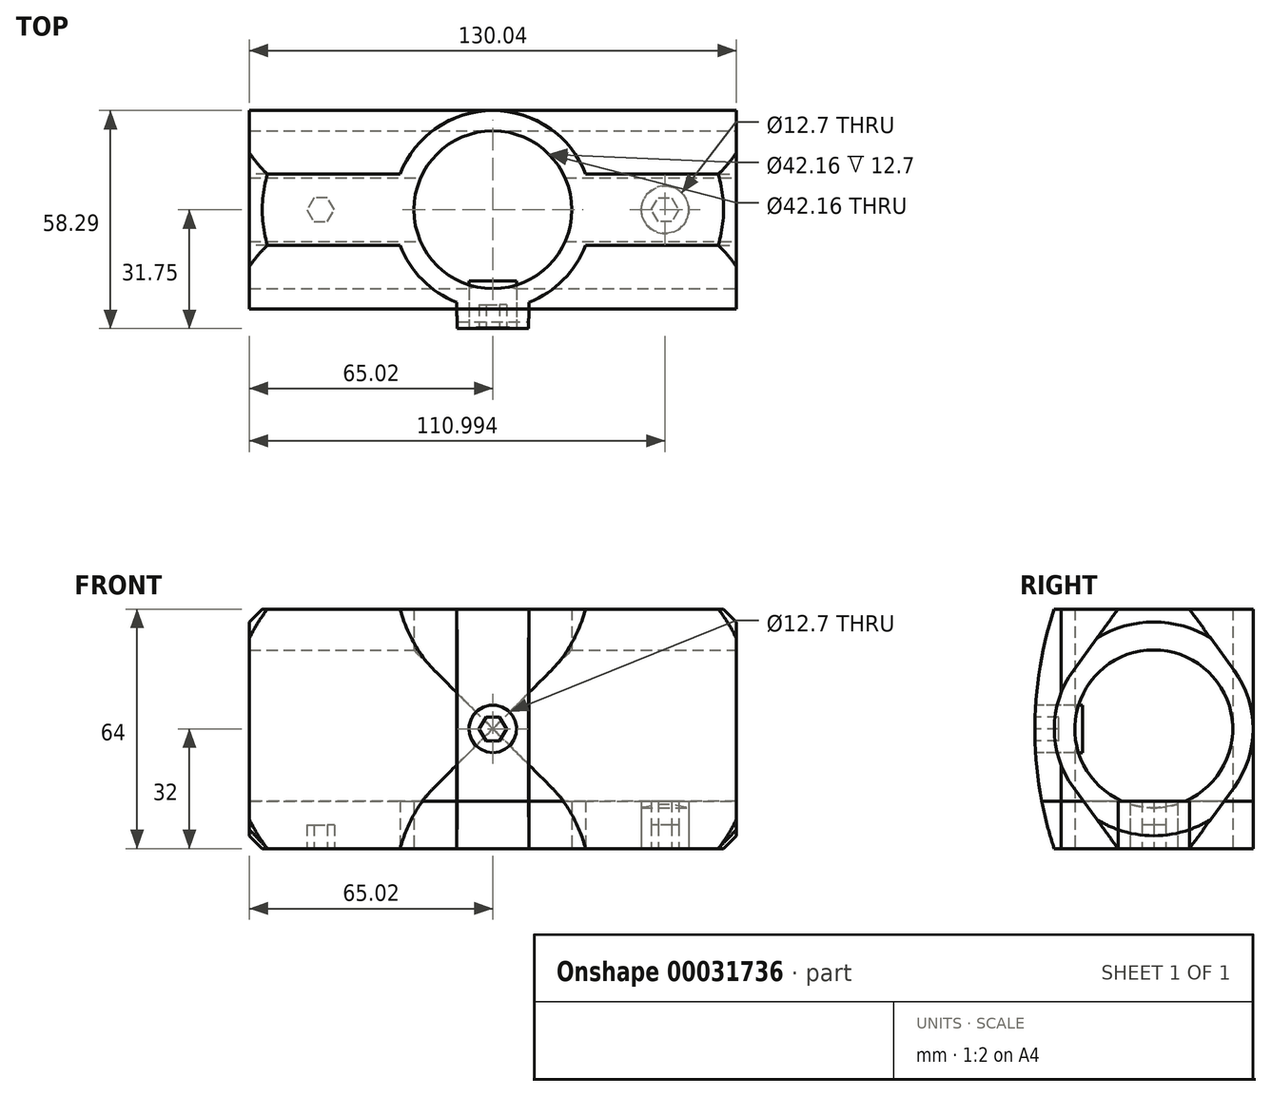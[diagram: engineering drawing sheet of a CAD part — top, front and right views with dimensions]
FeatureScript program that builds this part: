
annotation { "Feature Type Name" : "Feature", "Feature Type Description" : "" }
export const myFeature = defineFeature(function(context is Context, id is Id, definition is map)
    precondition{}
    {
        {
            var Q0;
            Q0=qCreatedBy(makeId("Right.planeOp"),FACE);
            var sketch = newSketch(context, id + "F0", { "sketchPlane" : qUnion([Q0])});
            skCircle(sketch, "E0", {"center": v(0, 0) * mm, "radius": 21.08 * mm});
            skCircle(sketch, "E1", {"center": v(0, 0) * mm, "radius": 26.54 * mm});
            skLineSegment(sketch, "E2.rect.bottom", {"start": v(9.53, 32) * mm, "end": v(-9.53, 32) * mm});
            skLineSegment(sketch, "E2.rect.top", {"start": v(9.53, -32) * mm, "end": v(-9.53, -32) * mm});
            skLineSegment(sketch, "E2.rect.left", {"start": v(9.53, 32) * mm, "end": v(9.53, -32) * mm});
            skLineSegment(sketch, "E2.rect.right", {"start": v(-9.53, 32) * mm, "end": v(-9.53, -32) * mm});
            skLineSegment(sketch, "E3", {"start": v(-9.53, 32) * mm, "end": v(-21.45, 15.63) * mm});
            skLineSegment(sketch, "E4", {"start": v(9.52, 32) * mm, "end": v(21.45, 15.63) * mm});
            skLineSegment(sketch, "E5", {"start": v(-9.52, -32) * mm, "end": v(-21.45, -15.63) * mm});
            skLineSegment(sketch, "E6", {"start": v(9.52, -32) * mm, "end": v(21.45, -15.63) * mm});
            skSolve(sketch);
        }
        {
            var Q0;
            {var subQ0=sQuery(id+"F0.wireOp",EDGE,"E2.rect.right");var subQ1=sQuery(id+"F0.wireOp",EDGE,"E0");var subQ3=makeQuery(id+"F0.imprint","INTERSECT",VERTEX,{"disambiguationData":[OD(0.0)],"derivedFrom":[subQ1,subQ0]});Q0=makeQuery(id+"F0.imprint","IMPRINT",FACE,{"disambiguationData":[TD([[makeQuery(id+"F0.imprint","IMPRINT",EDGE,{"disambiguationData":[TD([[subQ3,1.0]])],"derivedFrom":subQ1}),1.0]])]});}
            var Q1;
            {var subQ0=sQuery(id+"F0.wireOp",EDGE,"E2.rect.right");var subQ1=sQuery(id+"F0.wireOp",EDGE,"E0");var subQ3=makeQuery(id+"F0.imprint","INTERSECT",VERTEX,{"disambiguationData":[OD(0.0)],"derivedFrom":[subQ1,subQ0]});Q1=makeQuery(id+"F0.imprint","IMPRINT",FACE,{"disambiguationData":[TD([[makeQuery(id+"F0.imprint","IMPRINT",EDGE,{"disambiguationData":[TD([[subQ3,-1.0]])],"derivedFrom":subQ1}),1.0]])]});}
            var Q2;
            {var subQ0=sQuery(id+"F0.wireOp",EDGE,"E2.rect.right");var subQ3=sQuery(id+"F0.wireOp",EDGE,"E0");var subQ4=makeQuery(id+"F0.imprint","INTERSECT",VERTEX,{"disambiguationData":[OD(0.0)],"derivedFrom":[subQ3,subQ0]});Q2=makeQuery(id+"F0.imprint","IMPRINT",FACE,{"disambiguationData":[TD([[makeQuery(id+"F0.imprint","IMPRINT",EDGE,{"disambiguationData":[TD([[subQ4,-1.0]])],"derivedFrom":subQ3}),-1.0]])]});}
            var Q3;
            {var subQ0=sQuery(id+"F0.wireOp",EDGE,"E5");Q3=makeQuery(id+"F0.imprint","IMPRINT",FACE,{"disambiguationData":[TD([[makeQuery(id+"F0.imprint","IMPRINT",EDGE,{"derivedFrom":subQ0}),-1.0]])]});}
            var Q4;
            {var subQ3=sQuery(id+"F0.wireOp",EDGE,"E2.rect.top");Q4=makeQuery(id+"F0.imprint","IMPRINT",FACE,{"disambiguationData":[TD([[makeQuery(id+"F0.imprint","IMPRINT",EDGE,{"derivedFrom":subQ3}),-1.0]])]});}
            var Q5;
            {var subQ0=sQuery(id+"F0.wireOp",EDGE,"E2.rect.right");var subQ3=sQuery(id+"F0.wireOp",EDGE,"E0");var subQ4=makeQuery(id+"F0.imprint","INTERSECT",VERTEX,{"disambiguationData":[OD(1.0)],"derivedFrom":[subQ3,subQ0]});Q5=makeQuery(id+"F0.imprint","IMPRINT",FACE,{"disambiguationData":[TD([[makeQuery(id+"F0.imprint","IMPRINT",EDGE,{"disambiguationData":[TD([[subQ4,-1.0]])],"derivedFrom":subQ3}),-1.0]])]});}
            var Q6;
            {var subQ0=sQuery(id+"F0.wireOp",EDGE,"E6");Q6=makeQuery(id+"F0.imprint","IMPRINT",FACE,{"disambiguationData":[TD([[makeQuery(id+"F0.imprint","IMPRINT",EDGE,{"derivedFrom":subQ0}),1.0]])]});}
            var Q7;
            {var subQ0=sQuery(id+"F0.wireOp",EDGE,"E2.rect.left");var subQ3=sQuery(id+"F0.wireOp",EDGE,"E0");var subQ4=makeQuery(id+"F0.imprint","INTERSECT",VERTEX,{"disambiguationData":[OD(0.0)],"derivedFrom":[subQ3,subQ0]});Q7=makeQuery(id+"F0.imprint","IMPRINT",FACE,{"disambiguationData":[TD([[makeQuery(id+"F0.imprint","IMPRINT",EDGE,{"disambiguationData":[TD([[subQ4,1.0]])],"derivedFrom":subQ3}),-1.0]])]});}
            var Q8;
            {var subQ0=sQuery(id+"F0.wireOp",EDGE,"E2.rect.left");var subQ1=sQuery(id+"F0.wireOp",EDGE,"E0");var subQ3=makeQuery(id+"F0.imprint","INTERSECT",VERTEX,{"disambiguationData":[OD(0.0)],"derivedFrom":[subQ1,subQ0]});Q8=makeQuery(id+"F0.imprint","IMPRINT",FACE,{"disambiguationData":[TD([[makeQuery(id+"F0.imprint","IMPRINT",EDGE,{"disambiguationData":[TD([[subQ3,1.0]])],"derivedFrom":subQ1}),1.0]])]});}
            var Q9;
            {var subQ0=sQuery(id+"F0.wireOp",EDGE,"E2.rect.right");var subQ3=sQuery(id+"F0.wireOp",EDGE,"E0");var subQ4=makeQuery(id+"F0.imprint","INTERSECT",VERTEX,{"disambiguationData":[OD(0.0)],"derivedFrom":[subQ3,subQ0]});Q9=makeQuery(id+"F0.imprint","IMPRINT",FACE,{"disambiguationData":[TD([[makeQuery(id+"F0.imprint","IMPRINT",EDGE,{"disambiguationData":[TD([[subQ4,1.0]])],"derivedFrom":subQ3}),-1.0]])]});}
            var Q10;
            {var subQ0=sQuery(id+"F0.wireOp",EDGE,"E4");Q10=makeQuery(id+"F0.imprint","IMPRINT",FACE,{"disambiguationData":[TD([[makeQuery(id+"F0.imprint","IMPRINT",EDGE,{"derivedFrom":subQ0}),-1.0]])]});}
            var Q11;
            {var subQ3=sQuery(id+"F0.wireOp",EDGE,"E2.rect.bottom");Q11=makeQuery(id+"F0.imprint","IMPRINT",FACE,{"disambiguationData":[TD([[makeQuery(id+"F0.imprint","IMPRINT",EDGE,{"derivedFrom":subQ3}),1.0]])]});}
            var Q12;
            {var subQ0=sQuery(id+"F0.wireOp",EDGE,"E3");Q12=makeQuery(id+"F0.imprint","IMPRINT",FACE,{"disambiguationData":[TD([[makeQuery(id+"F0.imprint","IMPRINT",EDGE,{"derivedFrom":subQ0}),1.0]])]});}
            extrude(context, id + "F1", {"entities" : qUnion([Q0, Q1, Q2, Q3, Q4, Q5, Q6, Q7, Q8, Q9, Q10, Q11, Q12]), "endBound" : BoundingType.SYMMETRIC, "depth" : 130.05 * mm});
        }
        {
            var Q0;
            Q0=qCreatedBy(makeId("Top.planeOp"),FACE);
            var sketch = newSketch(context, id + "F2", { "sketchPlane" : qUnion([Q0])});
            skCircle(sketch, "E7", {"center": v(0, 0) * mm, "radius": 26.54 * mm});
            skCircle(sketch, "E8", {"center": v(0, 0) * mm, "radius": 21.08 * mm});
            skLineSegment(sketch, "E9", {"start": v(0, -31.75) * mm, "end": v(-9.53, -31.75) * mm});
            skLineSegment(sketch, "E10", {"start": v(-9.53, -31.75) * mm, "end": v(-9.67, -24.72) * mm});
            skLineSegment(sketch, "E11", {"start": v(-9.67, -24.72) * mm, "end": v(0, -24.72) * mm});
            skLineSegment(sketch, "E12.MirrorCS", {"start": v(0, -31.75) * mm, "end": v(9.53, -31.75) * mm});
            skLineSegment(sketch, "E13.MirrorCS", {"start": v(9.52, -31.75) * mm, "end": v(9.67, -24.72) * mm});
            skLineSegment(sketch, "E14.MirrorCS", {"start": v(9.67, -24.72) * mm, "end": v(0, -24.72) * mm});
            skSolve(sketch);
        }
        {
            var Q0;
            Q0=makeQuery(id+"F2.imprint","IMPRINT",FACE,{"disambiguationData":[TD([[makeQuery(id+"F2.imprint","IMPRINT",EDGE,{"derivedFrom":sQuery(id+"F2.wireOp",EDGE,"E9")}),-1.0]])]});
            var Q1;
            {var subQ1=sQuery(id+"F2.wireOp",EDGE,"E11");Q1=makeQuery(id+"F2.imprint","IMPRINT",FACE,{"disambiguationData":[TD([[makeQuery(id+"F2.imprint","IMPRINT",EDGE,{"derivedFrom":subQ1}),-1.0]])]});}
            var Q2;
            Q2=makeQuery(id+"F2.imprint","IMPRINT",FACE,{"disambiguationData":[TD([[makeQuery(id+"F2.imprint","IMPRINT",EDGE,{"derivedFrom":sQuery(id+"F2.wireOp",EDGE,"E8")}),-1.0]])]});
            var Q3;
            Q3=makeQuery(id+"F2.imprint","IMPRINT",FACE,{"disambiguationData":[TD([[makeQuery(id+"F2.imprint","IMPRINT",EDGE,{"derivedFrom":sQuery(id+"F2.wireOp",EDGE,"E8")}),1.0]])]});
            var Q4;
            Q4=makeQuery(id+"F1.opExtrude","SWEPT_FACE",FACE,{"disambiguationData":[OSD([sQuery(id+"F0.wireOp",EDGE,"E2.rect.bottom")])]});
            var Q5;
            Q5=makeQuery(id+"F1.opExtrude","SWEPT_FACE",FACE,{"disambiguationData":[OSD([sQuery(id+"F0.wireOp",EDGE,"E2.rect.top")])]});
            extrude(context, id + "F3", {"entities" : qUnion([Q0, Q1, Q2, Q3]), "operationType" : NewBodyOperationType.ADD, "endBound" : BoundingType.UP_TO_SURFACE, "endBoundEntityFace" : qUnion([Q4]), "depth" : 25.4 * mm, "hasSecondDirection" : true, "secondDirectionBound" : SecondDirectionBoundingType.UP_TO_SURFACE, "secondDirectionOppositeDirection" : true, "secondDirectionBoundEntityFace" : qUnion([Q5]), "secondDirectionDepth" : 25.4 * mm});
        }
        {
            var Q0;
            {var subQ0=sQuery(id+"F0.wireOp",EDGE,"E2.rect.left");var subQ1=sQuery(id+"F0.wireOp",EDGE,"E0");var subQ3=makeQuery(id+"F0.imprint","INTERSECT",VERTEX,{"disambiguationData":[OD(0.0)],"derivedFrom":[subQ1,subQ0]});Q0=makeQuery(id+"F0.imprint","IMPRINT",FACE,{"disambiguationData":[TD([[makeQuery(id+"F0.imprint","IMPRINT",EDGE,{"disambiguationData":[TD([[subQ3,1.0]])],"derivedFrom":subQ1}),1.0]])]});}
            var Q1;
            {var subQ0=sQuery(id+"F0.wireOp",EDGE,"E2.rect.right");var subQ1=sQuery(id+"F0.wireOp",EDGE,"E0");var subQ3=makeQuery(id+"F0.imprint","INTERSECT",VERTEX,{"disambiguationData":[OD(0.0)],"derivedFrom":[subQ1,subQ0]});Q1=makeQuery(id+"F0.imprint","IMPRINT",FACE,{"disambiguationData":[TD([[makeQuery(id+"F0.imprint","IMPRINT",EDGE,{"disambiguationData":[TD([[subQ3,1.0]])],"derivedFrom":subQ1}),1.0]])]});}
            var Q2;
            {var subQ0=sQuery(id+"F0.wireOp",EDGE,"E2.rect.right");var subQ1=sQuery(id+"F0.wireOp",EDGE,"E0");var subQ3=makeQuery(id+"F0.imprint","INTERSECT",VERTEX,{"disambiguationData":[OD(0.0)],"derivedFrom":[subQ1,subQ0]});Q2=makeQuery(id+"F0.imprint","IMPRINT",FACE,{"disambiguationData":[TD([[makeQuery(id+"F0.imprint","IMPRINT",EDGE,{"disambiguationData":[TD([[subQ3,-1.0]])],"derivedFrom":subQ1}),1.0]])]});}
            extrude(context, id + "F4", {"entities" : qUnion([Q0, Q1, Q2]), "operationType" : NewBodyOperationType.REMOVE, "endBound" : BoundingType.THROUGH_ALL, "oppositeDirection" : true, "depth" : 25.4 * mm, "hasSecondDirection" : true, "secondDirectionBound" : SecondDirectionBoundingType.THROUGH_ALL, "secondDirectionOppositeDirection" : false, "secondDirectionDepth" : 25.4 * mm});
        }
        {
            var Q0;
            Q0=makeQuery(id+"F2.imprint","IMPRINT",FACE,{"disambiguationData":[TD([[makeQuery(id+"F2.imprint","IMPRINT",EDGE,{"derivedFrom":sQuery(id+"F2.wireOp",EDGE,"E8")}),1.0]])]});
            extrude(context, id + "F5", {"entities" : qUnion([Q0]), "operationType" : NewBodyOperationType.REMOVE, "endBound" : BoundingType.THROUGH_ALL, "depth" : 25.4 * mm, "hasSecondDirection" : true, "secondDirectionBound" : SecondDirectionBoundingType.THROUGH_ALL, "secondDirectionOppositeDirection" : true, "secondDirectionDepth" : 25.4 * mm});
        }
        {
            var Q0;
            Q0=makeQuery(id+"F3.opExtrude","SWEPT_FACE",FACE,{"disambiguationData":[OSD([sQuery(id+"F2.wireOp",EDGE,"E9"),sQuery(id+"F2.wireOp",EDGE,"E12.MirrorCS")])]});
            var sketch = newSketch(context, id + "F6", { "sketchPlane" : qUnion([Q0])});
            skCircle(sketch, "E15", {"center": v(0, 0) * mm, "radius": 6.35 * mm});
            skCircle(sketch, "E16.cCircle", {"center": v(0, 0) * mm, "radius": 3.18 * mm, "construction": true});
            skLineSegment(sketch, "E16.0", {"start": v(-1.83, 3.18) * mm, "end": v(1.83, 3.18) * mm});
            skLineSegment(sketch, "E16.1", {"start": v(1.83, 3.18) * mm, "end": v(3.67, 0) * mm});
            skLineSegment(sketch, "E16.2", {"start": v(3.67, 0) * mm, "end": v(1.83, -3.18) * mm});
            skLineSegment(sketch, "E16.3", {"start": v(1.83, -3.18) * mm, "end": v(-1.83, -3.18) * mm});
            skLineSegment(sketch, "E16.4", {"start": v(-1.83, -3.18) * mm, "end": v(-3.67, 0) * mm});
            skLineSegment(sketch, "E16.5", {"start": v(-3.67, 0) * mm, "end": v(-1.83, 3.18) * mm});
            skPoint(sketch, "E16.0.midPoint", {"position": v(0, 3.18) * mm});
            skSolve(sketch);
        }
        {
            var Q0;
            Q0=makeQuery(id+"F6.imprint","IMPRINT",FACE,{"disambiguationData":[TD([[makeQuery(id+"F6.imprint","IMPRINT",EDGE,{"derivedFrom":sQuery(id+"F6.wireOp",EDGE,"E16.0")}),-1.0]])]});
            var Q1;
            Q1=makeQuery(id+"F6.imprint","IMPRINT",FACE,{"disambiguationData":[TD([[makeQuery(id+"F6.imprint","IMPRINT",EDGE,{"derivedFrom":sQuery(id+"F6.wireOp",EDGE,"E15")}),1.0]])]});
            extrude(context, id + "F7", {"entities" : qUnion([Q0, Q1]), "oppositeDirection" : true, "depth" : 12.7 * mm});
        }
        {
            var Q0;
            Q0=makeQuery(id+"F3.boolean.opBoolean","MERGE",FACE,{"derivedFrom":[makeQuery(id+"F1.opExtrude","SWEPT_FACE",FACE,{"disambiguationData":[OSD([sQuery(id+"F0.wireOp",EDGE,"E2.rect.top")])]}),makeQuery(id+"F3.opExtrude","CAP_FACE",FACE,{"disambiguationData":[OSD([sQuery(id+"F2.wireOp",EDGE,"E7"),sQuery(id+"F2.wireOp",EDGE,"E9"),sQuery(id+"F2.wireOp",EDGE,"E10"),sQuery(id+"F2.wireOp",EDGE,"E12.MirrorCS"),sQuery(id+"F2.wireOp",EDGE,"E13.MirrorCS")])],"isStart":true})]});
            var sketch = newSketch(context, id + "F8", { "sketchPlane" : qUnion([Q0])});
            skCircle(sketch, "E17", {"center": v(-45.97, 0) * mm, "radius": 6.35 * mm});
            skCircle(sketch, "E18.cCircle", {"center": v(-45.97, 0) * mm, "radius": 3.18 * mm, "construction": true});
            skLineSegment(sketch, "E18.0", {"start": v(-47.8, 3.18) * mm, "end": v(-44.14, 3.18) * mm});
            skLineSegment(sketch, "E18.1", {"start": v(-44.14, 3.18) * mm, "end": v(-42.3, 0) * mm});
            skLineSegment(sketch, "E18.2", {"start": v(-42.3, 0) * mm, "end": v(-44.14, -3.18) * mm});
            skLineSegment(sketch, "E18.3", {"start": v(-44.14, -3.17) * mm, "end": v(-47.8, -3.18) * mm});
            skLineSegment(sketch, "E18.4", {"start": v(-47.8, -3.18) * mm, "end": v(-49.64, 0) * mm});
            skLineSegment(sketch, "E18.5", {"start": v(-49.64, 0) * mm, "end": v(-47.8, 3.17) * mm});
            skPoint(sketch, "E18.0.midPoint", {"position": v(-45.97, 3.18) * mm});
            skCircle(sketch, "E19.MirrorC", {"center": v(45.97, 0) * mm, "radius": 6.35 * mm});
            skLineSegment(sketch, "E20.MirrorCS", {"start": v(47.8, 3.18) * mm, "end": v(44.14, 3.18) * mm});
            skLineSegment(sketch, "E21.MirrorCS", {"start": v(44.14, 3.18) * mm, "end": v(42.3, 0) * mm});
            skLineSegment(sketch, "E22.MirrorCS", {"start": v(42.3, 0) * mm, "end": v(44.14, -3.18) * mm});
            skLineSegment(sketch, "E23.MirrorCS", {"start": v(44.14, -3.17) * mm, "end": v(47.8, -3.17) * mm});
            skLineSegment(sketch, "E24.MirrorCS", {"start": v(47.8, -3.18) * mm, "end": v(49.64, 0) * mm});
            skLineSegment(sketch, "E25.MirrorCS", {"start": v(49.64, 0) * mm, "end": v(47.8, 3.18) * mm});
            skSolve(sketch);
        }
        {
            var Q0;
            Q0=makeQuery(id+"F8.imprint","IMPRINT",FACE,{"disambiguationData":[TD([[makeQuery(id+"F8.imprint","IMPRINT",EDGE,{"derivedFrom":sQuery(id+"F8.wireOp",EDGE,"E18.0")}),-1.0]])]});
            var Q1;
            Q1=makeQuery(id+"F8.imprint","IMPRINT",FACE,{"disambiguationData":[TD([[makeQuery(id+"F8.imprint","IMPRINT",EDGE,{"derivedFrom":sQuery(id+"F8.wireOp",EDGE,"E17")}),1.0]])]});
            var Q2;
            Q2=makeQuery(id+"F8.imprint","IMPRINT",FACE,{"disambiguationData":[TD([[makeQuery(id+"F8.imprint","IMPRINT",EDGE,{"derivedFrom":sQuery(id+"F8.wireOp",EDGE,"E20.MirrorCS")}),1.0]])]});
            var Q3;
            Q3=makeQuery(id+"F8.imprint","IMPRINT",FACE,{"disambiguationData":[TD([[makeQuery(id+"F8.imprint","IMPRINT",EDGE,{"derivedFrom":sQuery(id+"F8.wireOp",EDGE,"E19.MirrorC")}),-1.0]])]});
            extrude(context, id + "F9", {"entities" : qUnion([Q0, Q1, Q2, Q3]), "oppositeDirection" : true, "depth" : 12.7 * mm});
        }
        {
            var Q0;
            Q0=makeQuery(id+"F9.opExtrude","SWEPT_BODY",BODY,{"disambiguationData":[OSD([sQuery(id+"F8.wireOp",EDGE,"E17")])]});
            var Q1;
            Q1=makeQuery(id+"F9.opExtrude","SWEPT_BODY",BODY,{"disambiguationData":[OSD([sQuery(id+"F8.wireOp",EDGE,"E19.MirrorC")])]});
            var Q2;
            Q2=makeQuery(id+"F7.opExtrude","SWEPT_BODY",BODY,{"disambiguationData":[OSD([sQuery(id+"F6.wireOp",EDGE,"E15")])]});
            var Q3;
            Q3=makeQuery(id+"F1.opExtrude","SWEPT_BODY",BODY,{"disambiguationData":[OSD([sQuery(id+"F0.wireOp",EDGE,"E1"),sQuery(id+"F0.wireOp",EDGE,"E2.rect.bottom"),sQuery(id+"F0.wireOp",EDGE,"E2.rect.top"),sQuery(id+"F0.wireOp",EDGE,"E3"),sQuery(id+"F0.wireOp",EDGE,"E4"),sQuery(id+"F0.wireOp",EDGE,"E5"),sQuery(id+"F0.wireOp",EDGE,"E6")])]});
            booleanBodies(context, id + "F10", {"operationType" : BooleanOperationType.SUBTRACTION, "tools" : qUnion([Q0, Q1, Q2]), "targets" : qUnion([Q3]), "keepTools" : true});
        }
        {
            var Q0;
            Q0=makeQuery(id+"F6.imprint","IMPRINT",FACE,{"disambiguationData":[TD([[makeQuery(id+"F6.imprint","IMPRINT",EDGE,{"derivedFrom":sQuery(id+"F6.wireOp",EDGE,"E16.0")}),-1.0]])]});
            extrude(context, id + "F11", {"entities" : qUnion([Q0]), "operationType" : NewBodyOperationType.REMOVE, "oppositeDirection" : true, "depth" : 6.35 * mm});
        }
        {
            var Q0;
            Q0=makeQuery(id+"F8.imprint","IMPRINT",FACE,{"disambiguationData":[TD([[makeQuery(id+"F8.imprint","IMPRINT",EDGE,{"derivedFrom":sQuery(id+"F8.wireOp",EDGE,"E18.0")}),-1.0]])]});
            var Q1;
            Q1=makeQuery(id+"F8.imprint","IMPRINT",FACE,{"disambiguationData":[TD([[makeQuery(id+"F8.imprint","IMPRINT",EDGE,{"derivedFrom":sQuery(id+"F8.wireOp",EDGE,"E20.MirrorCS")}),1.0]])]});
            extrude(context, id + "F12", {"entities" : qUnion([Q0, Q1]), "operationType" : NewBodyOperationType.REMOVE, "oppositeDirection" : true, "depth" : 6.35 * mm});
        }
        {
            var Q0;
            Q0=qCreatedBy(makeId("Right.planeOp"),FACE);
            var sketch = newSketch(context, id + "F13", { "sketchPlane" : qUnion([Q0])});
            skArc(sketch, "E26", {"start": v(-26.58, 32) * mm, "mid": v(-31.75, 0) * mm, "end": v(-26.58, -32) * mm});
            skLineSegment(sketch, "E27", {"start": v(-26.58, -32) * mm, "end": v(-38.1, -32) * mm});
            skLineSegment(sketch, "E28", {"start": v(-38.1, -32) * mm, "end": v(-38.1, 32) * mm});
            skLineSegment(sketch, "E29", {"start": v(-38.1, 32) * mm, "end": v(-26.58, 32) * mm});
            skSolve(sketch);
        }
        {
            var Q0;
            Q0=makeQuery(id+"F13.imprint","IMPRINT",FACE,{"disambiguationData":[TD([[makeQuery(id+"F13.imprint","IMPRINT",EDGE,{"derivedFrom":sQuery(id+"F13.wireOp",EDGE,"E26")}),-1.0]])]});
            extrude(context, id + "F14", {"entities" : qUnion([Q0]), "operationType" : NewBodyOperationType.REMOVE, "endBound" : BoundingType.THROUGH_ALL, "oppositeDirection" : true, "depth" : 25.4 * mm, "hasSecondDirection" : true, "secondDirectionBound" : SecondDirectionBoundingType.THROUGH_ALL, "secondDirectionOppositeDirection" : false, "secondDirectionDepth" : 25.4 * mm});
        }
        {
            var Q0;
            Q0=qCreatedBy(makeId("Front.planeOp"),FACE);
            var sketch = newSketch(context, id + "F15", { "sketchPlane" : qUnion([Q0])});
            skLineSegment(sketch, "E30", {"start": v(-93.6, 0) * mm, "end": v(-55.25, 38.35) * mm});
            skLineSegment(sketch, "E31", {"start": v(-55.25, 38.35) * mm, "end": v(-99.95, 38.35) * mm});
            skLineSegment(sketch, "E32", {"start": v(-99.95, 38.35) * mm, "end": v(-99.95, 0) * mm});
            skLineSegment(sketch, "E33", {"start": v(-99.95, 0) * mm, "end": v(-93.6, 0) * mm});
            skLineSegment(sketch, "E34.MirrorCS", {"start": v(93.6, 0) * mm, "end": v(55.25, 38.35) * mm});
            skLineSegment(sketch, "E35.MirrorCS", {"start": v(55.25, 38.35) * mm, "end": v(99.95, 38.35) * mm});
            skLineSegment(sketch, "E36.MirrorCS", {"start": v(99.95, 0) * mm, "end": v(93.6, 0) * mm});
            skLineSegment(sketch, "E37.MirrorCS", {"start": v(99.95, 38.35) * mm, "end": v(99.95, 0) * mm});
            skSolve(sketch);
        }
        {
            var Q0;
            Q0=makeQuery(id+"F15.imprint","IMPRINT",FACE,{"disambiguationData":[TD([[makeQuery(id+"F15.imprint","IMPRINT",EDGE,{"derivedFrom":sQuery(id+"F15.wireOp",EDGE,"E30")}),1.0]])]});
            var Q1;
            Q1=makeQuery(id+"F15.imprint","IMPRINT",FACE,{"disambiguationData":[TD([[makeQuery(id+"F15.imprint","IMPRINT",EDGE,{"derivedFrom":sQuery(id+"F15.wireOp",EDGE,"E34.MirrorCS")}),-1.0]])]});
            var Q2;
            Q2=sQuery(id+"F15.wireOp",EDGE,"E33");
            revolve(context, id + "F16", {"operationType" : NewBodyOperationType.REMOVE, "entities" : qUnion([Q0, Q1]), "axis" : qUnion([Q2]), "revolveType" : RevolveType.FULL, "oppositeDirection" : true});
        }
    });
